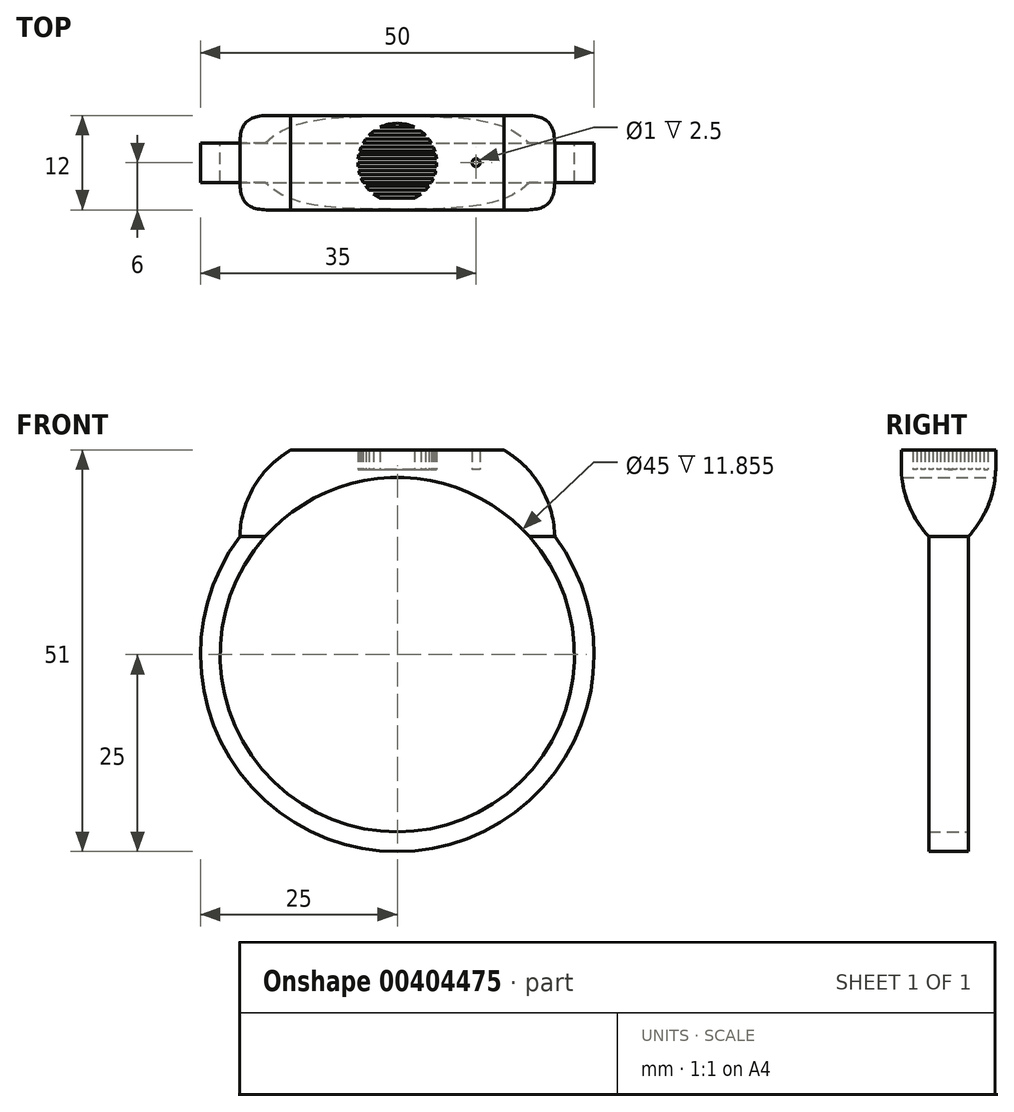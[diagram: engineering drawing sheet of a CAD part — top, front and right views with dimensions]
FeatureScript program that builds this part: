
annotation { "Feature Type Name" : "Feature", "Feature Type Description" : "" }
export const myFeature = defineFeature(function(context is Context, id is Id, definition is map)
    precondition{}
    {
        {
            var Q0;
            Q0=qCreatedBy(makeId("Front.planeOp"),FACE);
            var sketch = newSketch(context, id + "F0", { "sketchPlane" : qUnion([Q0])});
            skCircle(sketch, "E0", {"center": v(0, 0) * mm, "radius": 25 * mm});
            skCircle(sketch, "E1", {"center": v(0, 0) * mm, "radius": 22.5 * mm});
            skLineSegment(sketch, "E2", {"start": v(-20, 15) * mm, "end": v(-16.77, 15) * mm});
            skLineSegment(sketch, "E3", {"start": v(20, 15) * mm, "end": v(16.77, 15) * mm});
            skLineSegment(sketch, "E4", {"start": v(-20, 15) * mm, "end": v(-20, 20) * mm});
            skLineSegment(sketch, "E5", {"start": v(20, 15) * mm, "end": v(20, 20) * mm});
            skPoint(sketch, "E6", {"position": v(0, 22.5) * mm});
            skArc(sketch, "E7", {"start": v(20, 20) * mm, "mid": v(0, 30) * mm, "end": v(-20, 20) * mm});
            skLineSegment(sketch, "E8", {"start": v(-13.56, 26) * mm, "end": v(13.56, 26) * mm});
            skPoint(sketch, "E9", {"position": v(-13.56, 26) * mm});
            skPoint(sketch, "E10", {"position": v(13.56, 26) * mm});
            skSolve(sketch);
        }
        {
            var Q0;
            Q0=makeQuery(id+"F0.imprint","IMPRINT",FACE,{"disambiguationData":[TD([[makeQuery(id+"F0.imprint","IMPRINT",EDGE,{"derivedFrom":sQuery(id+"F0.wireOp",EDGE,"E1")}),-1.0]])]});
            extrude(context, id + "F1", {"entities" : qUnion([Q0]), "depth" : 2.5 * mm, "hasSecondDirection" : true, "secondDirectionOppositeDirection" : true, "secondDirectionDepth" : 2.5 * mm});
        }
        {
            var Q0;
            {var subQ0=sQuery(id+"F0.wireOp",EDGE,"E2");Q0=makeQuery(id+"F0.imprint","IMPRINT",FACE,{"disambiguationData":[TD([[makeQuery(id+"F0.imprint","IMPRINT",EDGE,{"derivedFrom":subQ0}),1.0]])]});}
            var Q1;
            {var subQ0=sQuery(id+"F0.wireOp",EDGE,"1f85ef3d-5dfe-47ac-9454-f6da41c13103");Q1=makeQuery(id+"F0.imprint","IMPRINT",FACE,{"disambiguationData":[TD([[makeQuery(id+"F0.imprint","IMPRINT",EDGE,{"derivedFrom":subQ0}),1.0]])]});}
            var Q2;
            {var subQ6=sQuery(id+"F0.wireOp",EDGE,"E4");Q2=makeQuery(id+"F0.imprint","IMPRINT",FACE,{"disambiguationData":[TD([[makeQuery(id+"F0.imprint","IMPRINT",EDGE,{"derivedFrom":subQ6}),-1.0]])]});}
            extrude(context, id + "F2", {"entities" : qUnion([Q0, Q1, Q2]), "operationType" : NewBodyOperationType.ADD, "depth" : 6 * mm, "hasSecondDirection" : true, "secondDirectionOppositeDirection" : true, "secondDirectionDepth" : 6 * mm});
        }
        {
            var Q0;
            Q0=makeQuery(id+"F2.opExtrude","SWEPT_EDGE",EDGE,{"disambiguationData":[OSD([sQuery(id+"F0.wireOp",EDGE,"E4"),sQuery(id+"F0.wireOp",EDGE,"E7")])]});
            var Q1;
            Q1=makeQuery(id+"F2.opExtrude","SWEPT_EDGE",EDGE,{"disambiguationData":[OSD([sQuery(id+"F0.wireOp",EDGE,"E5"),sQuery(id+"F0.wireOp",EDGE,"E7")])]});
            fillet(context, id + "F3", {"entities" : qUnion([Q0, Q1]), "radius" : 13 * mm, "tangentPropagation" : true, "allowEdgeOverflow" : false});
        }
        {
            var Q0;
            Q0=makeQuery(id+"F2.opExtrude","CAP_EDGE",EDGE,{"disambiguationData":[OSD([sQuery(id+"F0.wireOp",EDGE,"E3")])],"isStart":false});
            var Q1;
            Q1=makeQuery(id+"F2.opExtrude","CAP_EDGE",EDGE,{"disambiguationData":[OSD([sQuery(id+"F0.wireOp",EDGE,"E3")])],"isStart":true});
            fillet(context, id + "F4", {"entities" : qUnion([Q0, Q1]), "radius" : 13 * mm, "tangentPropagation" : true, "allowEdgeOverflow" : false});
        }
        {
            var Q0;
            Q0=qCreatedBy(makeId("Top.planeOp"),FACE);
            var sketch = newSketch(context, id + "F5", { "sketchPlane" : qUnion([Q0])});
            skCircle(sketch, "E11", {"center": v(0, 0) * mm, "radius": 5 * mm});
            skLineSegment(sketch, "E12", {"start": v(-5, 0) * mm, "end": v(5, 0) * mm});
            skLineSegment(sketch, "E13", {"start": v(-4.97, -0.5) * mm, "end": v(4.97, -0.5) * mm});
            skLineSegment(sketch, "E14", {"start": v(-4.9, -1) * mm, "end": v(4.9, -1) * mm});
            skLineSegment(sketch, "E15", {"start": v(-4.77, -1.5) * mm, "end": v(4.77, -1.5) * mm});
            skLineSegment(sketch, "E16", {"start": v(-4.58, -2) * mm, "end": v(4.58, -2) * mm});
            skLineSegment(sketch, "E17", {"start": v(-4.33, -2.5) * mm, "end": v(4.33, -2.5) * mm});
            skLineSegment(sketch, "E18", {"start": v(-4, -3) * mm, "end": v(4, -3) * mm});
            skLineSegment(sketch, "E19", {"start": v(-3.57, -3.5) * mm, "end": v(3.57, -3.5) * mm});
            skLineSegment(sketch, "E20", {"start": v(-3, -4) * mm, "end": v(3, -4) * mm});
            skLineSegment(sketch, "E21", {"start": v(-2.18, -4.5) * mm, "end": v(2.18, -4.5) * mm});
            skLineSegment(sketch, "E22", {"start": v(-4.97, 0.5) * mm, "end": v(4.97, 0.5) * mm});
            skLineSegment(sketch, "E23", {"start": v(-4.9, 1) * mm, "end": v(4.9, 1) * mm});
            skLineSegment(sketch, "E24", {"start": v(-4.77, 1.5) * mm, "end": v(4.77, 1.5) * mm});
            skLineSegment(sketch, "E25", {"start": v(-4.58, 2) * mm, "end": v(4.58, 2) * mm});
            skLineSegment(sketch, "E26", {"start": v(-4.33, 2.5) * mm, "end": v(4.33, 2.5) * mm});
            skLineSegment(sketch, "E27", {"start": v(-4, 3) * mm, "end": v(4, 3) * mm});
            skLineSegment(sketch, "E28", {"start": v(-3.57, 3.5) * mm, "end": v(3.57, 3.5) * mm});
            skLineSegment(sketch, "E29", {"start": v(-3, 4) * mm, "end": v(3, 4) * mm});
            skLineSegment(sketch, "E30", {"start": v(-2.18, 4.5) * mm, "end": v(2.18, 4.5) * mm});
            skLineSegment(sketch, "E31", {"start": v(0, 0) * mm, "end": v(10, 0) * mm});
            skCircle(sketch, "E32", {"center": v(10, 0) * mm, "radius": 0.5 * mm});
            skSolve(sketch);
        }
        {
            var Q0;
            Q0=makeQuery(id+"F5.imprint","IMPRINT",FACE,{"disambiguationData":[TD([[makeQuery(id+"F5.imprint","IMPRINT",EDGE,{"derivedFrom":sQuery(id+"F5.wireOp",EDGE,"E32")}),1.0]])]});
            var Q1;
            {var subQ0=sQuery(id+"F5.wireOp",EDGE,"E30");Q1=makeQuery(id+"F5.imprint","IMPRINT",FACE,{"disambiguationData":[TD([[makeQuery(id+"F5.imprint","IMPRINT",EDGE,{"derivedFrom":subQ0}),1.0]])]});}
            var Q2;
            {var subQ0=sQuery(id+"F5.wireOp",EDGE,"E22");Q2=makeQuery(id+"F5.imprint","IMPRINT",FACE,{"disambiguationData":[TD([[makeQuery(id+"F5.imprint","IMPRINT",EDGE,{"derivedFrom":subQ0}),1.0]])]});}
            var Q3;
            {var subQ0=sQuery(id+"F5.wireOp",EDGE,"E24");Q3=makeQuery(id+"F5.imprint","IMPRINT",FACE,{"disambiguationData":[TD([[makeQuery(id+"F5.imprint","IMPRINT",EDGE,{"derivedFrom":subQ0}),1.0]])]});}
            var Q4;
            {var subQ0=sQuery(id+"F5.wireOp",EDGE,"E26");Q4=makeQuery(id+"F5.imprint","IMPRINT",FACE,{"disambiguationData":[TD([[makeQuery(id+"F5.imprint","IMPRINT",EDGE,{"derivedFrom":subQ0}),1.0]])]});}
            var Q5;
            {var subQ0=sQuery(id+"F5.wireOp",EDGE,"E28");Q5=makeQuery(id+"F5.imprint","IMPRINT",FACE,{"disambiguationData":[TD([[makeQuery(id+"F5.imprint","IMPRINT",EDGE,{"derivedFrom":subQ0}),1.0]])]});}
            var Q6;
            {var subQ0=sQuery(id+"F5.wireOp",EDGE,"E12");Q6=makeQuery(id+"F5.imprint","IMPRINT",FACE,{"disambiguationData":[TD([[makeQuery(id+"F5.imprint","IMPRINT",EDGE,{"derivedFrom":subQ0}),-1.0]])]});}
            var Q7;
            {var subQ0=sQuery(id+"F5.wireOp",EDGE,"E14");Q7=makeQuery(id+"F5.imprint","IMPRINT",FACE,{"disambiguationData":[TD([[makeQuery(id+"F5.imprint","IMPRINT",EDGE,{"derivedFrom":subQ0}),-1.0]])]});}
            var Q8;
            {var subQ0=sQuery(id+"F5.wireOp",EDGE,"E16");Q8=makeQuery(id+"F5.imprint","IMPRINT",FACE,{"disambiguationData":[TD([[makeQuery(id+"F5.imprint","IMPRINT",EDGE,{"derivedFrom":subQ0}),-1.0]])]});}
            var Q9;
            {var subQ0=sQuery(id+"F5.wireOp",EDGE,"E18");Q9=makeQuery(id+"F5.imprint","IMPRINT",FACE,{"disambiguationData":[TD([[makeQuery(id+"F5.imprint","IMPRINT",EDGE,{"derivedFrom":subQ0}),-1.0]])]});}
            var Q10;
            {var subQ0=sQuery(id+"F5.wireOp",EDGE,"E20");Q10=makeQuery(id+"F5.imprint","IMPRINT",FACE,{"disambiguationData":[TD([[makeQuery(id+"F5.imprint","IMPRINT",EDGE,{"derivedFrom":subQ0}),-1.0]])]});}
            extrude(context, id + "F6", {"entities" : qUnion([Q0, Q1, Q2, Q3, Q4, Q5, Q6, Q7, Q8, Q9, Q10]), "operationType" : NewBodyOperationType.REMOVE, "depth" : 28.7 * mm, "hasSecondDirection" : true, "secondDirectionOppositeDirection" : false, "secondDirectionDepth" : 23.5 * mm});
        }
    });
